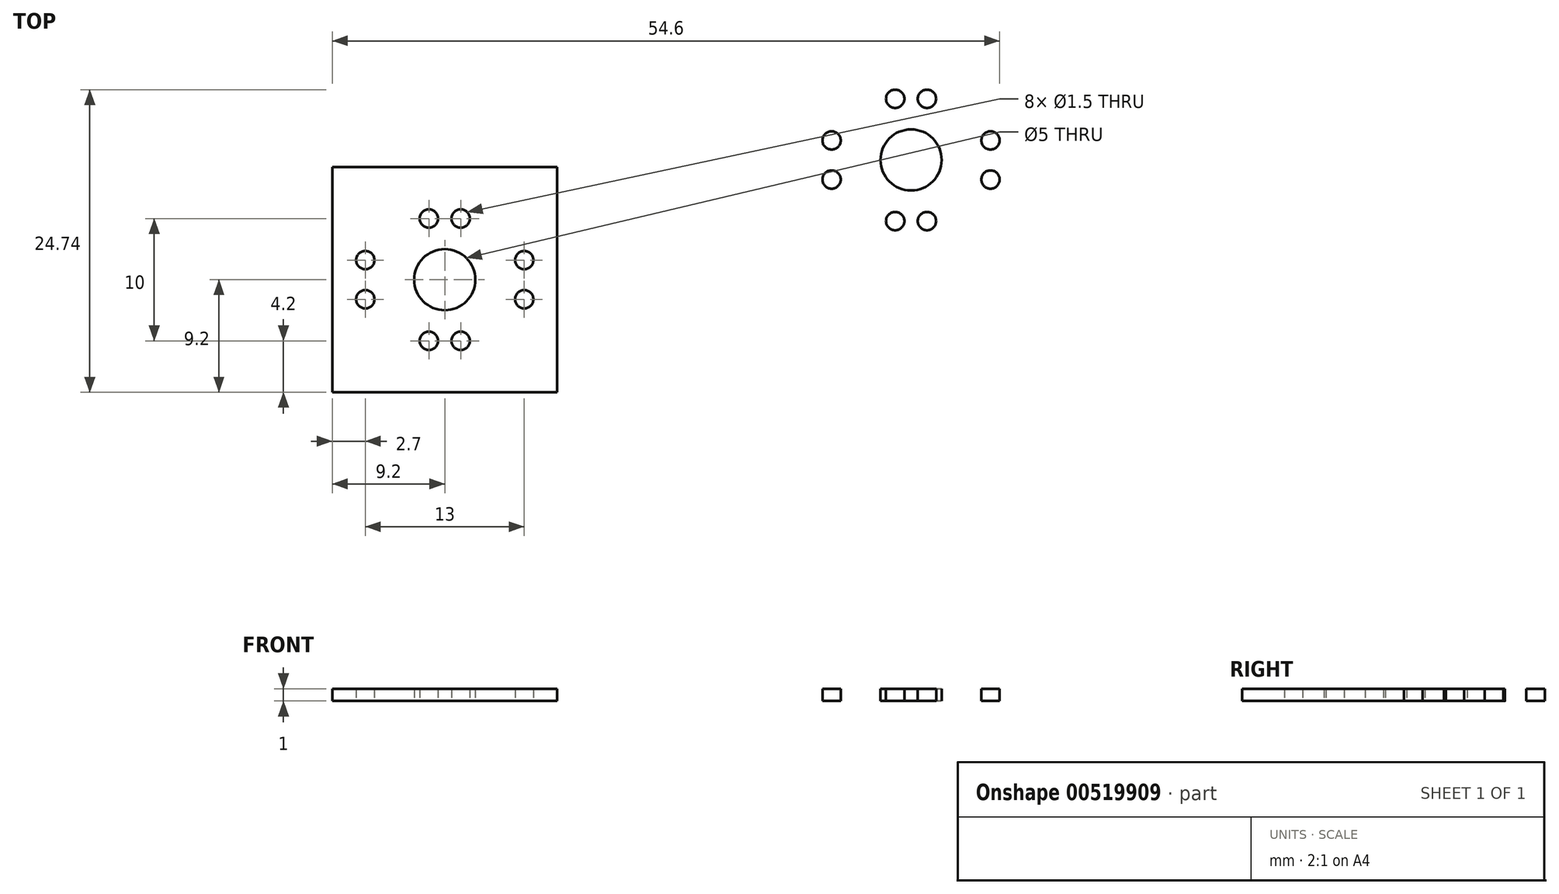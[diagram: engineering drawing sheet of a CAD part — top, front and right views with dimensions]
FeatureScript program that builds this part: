
annotation { "Feature Type Name" : "Feature", "Feature Type Description" : "" }
export const myFeature = defineFeature(function(context is Context, id is Id, definition is map)
    precondition{}
    {
        {
            var Q0;
            Q0=qCreatedBy(makeId("Top.planeOp"),FACE);
            var sketch = newSketch(context, id + "F0", { "sketchPlane" : qUnion([Q0])});
            skLineSegment(sketch, "E0", {"start": v(0, 53.65) * mm, "end": v(0, 0) * mm, "construction": true});
            skLineSegment(sketch, "E1", {"start": v(0, 0) * mm, "end": v(0, 9.2) * mm, "construction": true});
            skLineSegment(sketch, "E2", {"start": v(0, 9.2) * mm, "end": v(0, 4.2) * mm});
            skLineSegment(sketch, "E3", {"start": v(0, 4.2) * mm, "end": v(-1.3, 4.2) * mm, "construction": true});
            skCircle(sketch, "E4", {"center": v(-1.3, 4.2) * mm, "radius": 0.75 * mm});
            skLineSegment(sketch, "E5", {"start": v(0, 9.2) * mm, "end": v(-7.25, 9.2) * mm, "construction": true});
            skCircle(sketch, "E6.MirrorC", {"center": v(-1.3, 14.2) * mm, "radius": 0.75 * mm});
            skCircle(sketch, "E7.MirrorC", {"center": v(1.3, 14.2) * mm, "radius": 0.75 * mm});
            skCircle(sketch, "E8.MirrorC", {"center": v(1.3, 4.2) * mm, "radius": 0.75 * mm});
            skLineSegment(sketch, "E9", {"start": v(0, 9.2) * mm, "end": v(6.5, 9.2) * mm, "construction": true});
            skLineSegment(sketch, "E10", {"start": v(6.5, 9.2) * mm, "end": v(6.5, 7.6) * mm, "construction": true});
            skCircle(sketch, "E11", {"center": v(6.5, 7.6) * mm, "radius": 0.75 * mm});
            skCircle(sketch, "E12.MirrorC", {"center": v(6.5, 10.8) * mm, "radius": 0.75 * mm});
            skCircle(sketch, "E13.MirrorC", {"center": v(-6.5, 10.8) * mm, "radius": 0.75 * mm});
            skCircle(sketch, "E14.MirrorC", {"center": v(-6.5, 7.6) * mm, "radius": 0.75 * mm});
            skCircle(sketch, "E15", {"center": v(0, 9.2) * mm, "radius": 2.5 * mm});
            skLineSegment(sketch, "E16", {"start": v(0, 0) * mm, "end": v(-9.2, 0) * mm});
            skLineSegment(sketch, "E17", {"start": v(-9.2, 0) * mm, "end": v(-9.2, 18.4) * mm});
            skLineSegment(sketch, "E18", {"start": v(-9.2, 18.4) * mm, "end": v(0, 18.4) * mm});
            skLineSegment(sketch, "E19.MirrorCS", {"start": v(9.2, 0) * mm, "end": v(9.2, 18.4) * mm});
            skLineSegment(sketch, "E20.MirrorCS", {"start": v(9.2, 18.4) * mm, "end": v(0, 18.4) * mm});
            skLineSegment(sketch, "E21.MirrorCS", {"start": v(0, 0) * mm, "end": v(9.2, 0) * mm});
            skLineSegment(sketch, "E22", {"start": v(38.15, 9.8) * mm, "end": v(38.15, 19) * mm, "construction": true});
            skLineSegment(sketch, "E23", {"start": v(38.15, 19) * mm, "end": v(38.15, 14) * mm});
            skLineSegment(sketch, "E24", {"start": v(38.15, 14) * mm, "end": v(36.85, 14) * mm, "construction": true});
            skCircle(sketch, "E25", {"center": v(36.85, 14) * mm, "radius": 0.75 * mm});
            skLineSegment(sketch, "E26", {"start": v(38.15, 19) * mm, "end": v(30.9, 19) * mm, "construction": true});
            skCircle(sketch, "E27.MirrorC", {"center": v(36.85, 24) * mm, "radius": 0.75 * mm});
            skCircle(sketch, "E28.MirrorC", {"center": v(39.45, 24) * mm, "radius": 0.75 * mm});
            skCircle(sketch, "E29.MirrorC", {"center": v(39.45, 14) * mm, "radius": 0.75 * mm});
            skLineSegment(sketch, "E30", {"start": v(38.15, 19) * mm, "end": v(44.65, 19) * mm, "construction": true});
            skLineSegment(sketch, "E31", {"start": v(44.65, 19) * mm, "end": v(44.65, 17.4) * mm, "construction": true});
            skCircle(sketch, "E32", {"center": v(44.65, 17.4) * mm, "radius": 0.75 * mm});
            skCircle(sketch, "E33.MirrorC", {"center": v(44.65, 20.6) * mm, "radius": 0.75 * mm});
            skCircle(sketch, "E34.MirrorC", {"center": v(31.65, 20.6) * mm, "radius": 0.75 * mm});
            skCircle(sketch, "E35.MirrorC", {"center": v(31.65, 17.4) * mm, "radius": 0.75 * mm});
            skCircle(sketch, "E36", {"center": v(38.15, 19) * mm, "radius": 2.5 * mm});
            skSolve(sketch);
        }
        {
            var Q0;
            Q0 = qSketchRegion(id + "F0", true);
            extrude(context, id + "F1", {"entities" : qUnion([Q0]), "depth" : 1 * mm, "offsetDistance" : 25 * mm});
        }
    });
